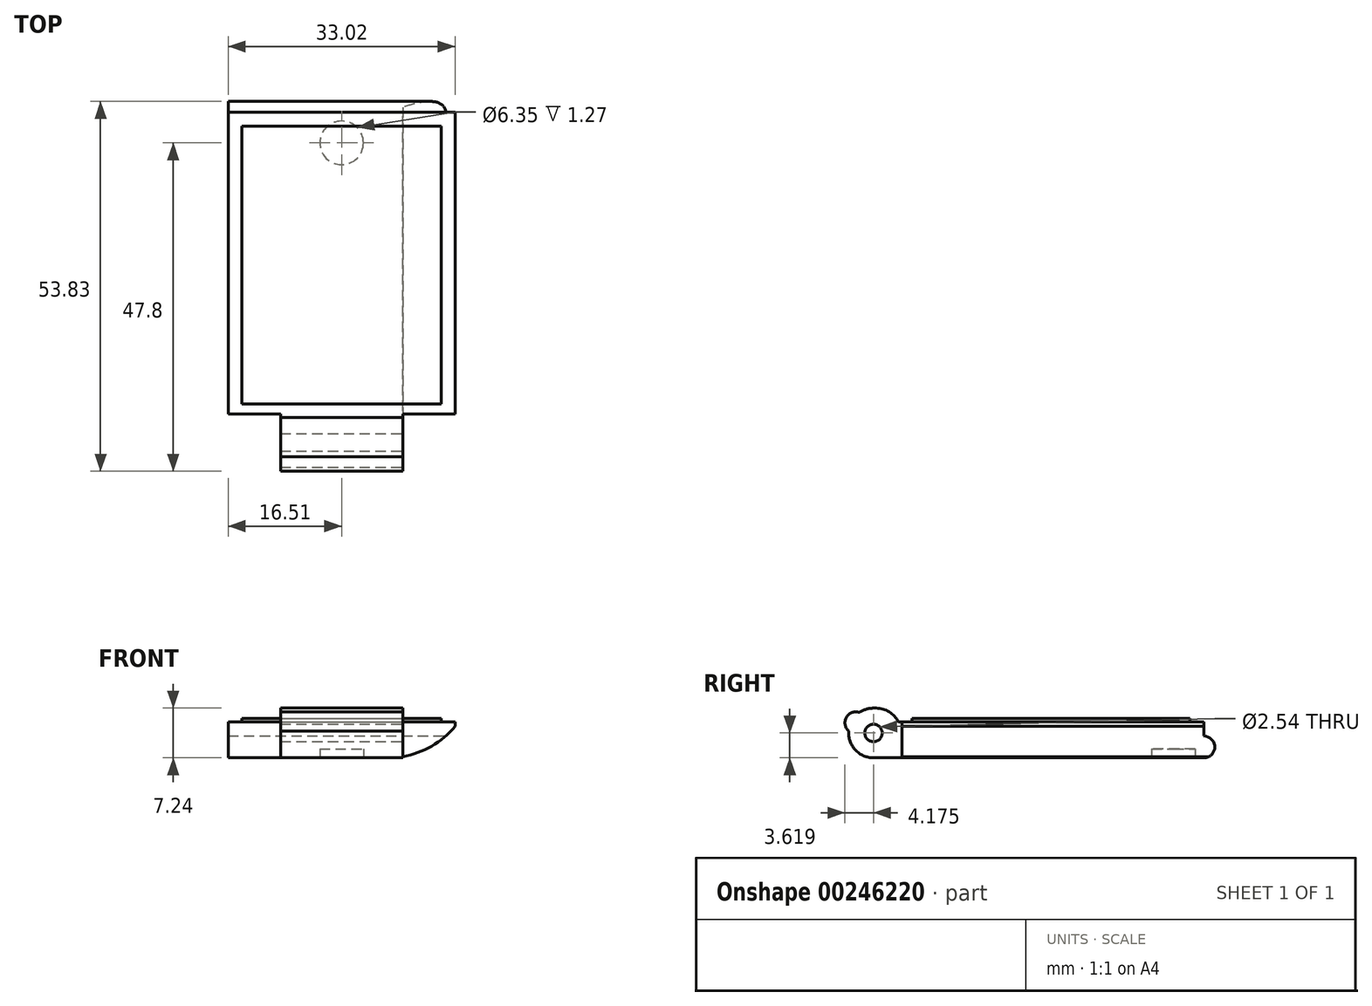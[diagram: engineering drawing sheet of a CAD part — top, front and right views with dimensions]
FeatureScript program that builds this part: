
annotation { "Feature Type Name" : "Feature", "Feature Type Description" : "" }
export const myFeature = defineFeature(function(context is Context, id is Id, definition is map)
    precondition{}
    {
        {
            var Q0;
            Q0=qCreatedBy(makeId("Top.planeOp"),FACE);
            var sketch = newSketch(context, id + "F0", { "sketchPlane" : qUnion([Q0])});
            skLineSegment(sketch, "E0.bottom", {"start": v(-16.51, 22.23) * mm, "end": v(16.51, 22.23) * mm});
            skLineSegment(sketch, "E0.top", {"start": v(-16.51, -22.23) * mm, "end": v(16.51, -22.23) * mm});
            skLineSegment(sketch, "E0.left", {"start": v(-16.51, 22.23) * mm, "end": v(-16.51, -22.23) * mm});
            skLineSegment(sketch, "E0.right", {"start": v(16.51, 22.23) * mm, "end": v(16.51, -22.23) * mm});
            skPoint(sketch, "E0.middle", {"position": v(0, 0) * mm});
            skSolve(sketch);
        }
        {
            var Q0;
            Q0 = qSketchRegion(id + "F0", true);
            extrude(context, id + "F1", {"entities" : qUnion([Q0]), "depth" : 5.7 * mm});
        }
        {
            var Q0;
            Q0=makeQuery(id+"F1.opExtrude","SWEPT_FACE",FACE,{"disambiguationData":[OSD([sQuery(id+"F0.wireOp",EDGE,"E0.top")])]});
            var sketch = newSketch(context, id + "F2", { "sketchPlane" : qUnion([Q0])});
            skLineSegment(sketch, "E1.bottom", {"start": v(-8.9, 7.24) * mm, "end": v(8.89, 7.24) * mm});
            skLineSegment(sketch, "E1.top", {"start": v(-8.9, 0) * mm, "end": v(8.9, 0) * mm});
            skLineSegment(sketch, "E1.left", {"start": v(-8.9, 7.24) * mm, "end": v(-8.9, 0) * mm});
            skLineSegment(sketch, "E1.right", {"start": v(8.9, 7.24) * mm, "end": v(8.9, 0) * mm});
            skSolve(sketch);
        }
        {
            var Q0;
            Q0 = qSketchRegion(id + "F2", true);
            extrude(context, id + "F3", {"entities" : qUnion([Q0]), "operationType" : NewBodyOperationType.ADD, "depth" : 7.24 * mm});
        }
        {
            var Q0;
            Q0=makeQuery(id+"F3.opExtrude","SWEPT_FACE",FACE,{"disambiguationData":[OSD([sQuery(id+"F2.wireOp",EDGE,"E1.right")])]});
            var sketch = newSketch(context, id + "F4", { "sketchPlane" : qUnion([Q0])});
            skCircle(sketch, "E2", {"center": v(-25.84, 3.62) * mm, "radius": 1.27 * mm});
            skPoint(sketch, "E2.centerSnap0", {"position": v(-29.46, 3.62) * mm});
            skPoint(sketch, "E2.centerSnap1", {"position": v(-25.84, 7.24) * mm});
            skSolve(sketch);
        }
        {
            var Q0;
            Q0 = qSketchRegion(id + "F4", true);
            extrude(context, id + "F5", {"entities" : qUnion([Q0]), "operationType" : NewBodyOperationType.REMOVE, "oppositeDirection" : true, "depth" : 19.05 * mm});
        }
        {
            var Q0;
            Q0=makeQuery(id+"F1.opExtrude","CAP_FACE",FACE,{"disambiguationData":[OSD([sQuery(id+"F0.wireOp",EDGE,"E0.bottom"),sQuery(id+"F0.wireOp",EDGE,"E0.top"),sQuery(id+"F0.wireOp",EDGE,"E0.left"),sQuery(id+"F0.wireOp",EDGE,"E0.right")])],"isStart":false});
            var sketch = newSketch(context, id + "F6", { "sketchPlane" : qUnion([Q0])});
            skLineSegment(sketch, "E3.bottom", {"start": v(-16.51, 22.23) * mm, "end": v(16.51, 22.23) * mm});
            skLineSegment(sketch, "E3.top", {"start": v(-16.51, -22.23) * mm, "end": v(16.51, -22.23) * mm});
            skLineSegment(sketch, "E3.left", {"start": v(-16.51, 22.23) * mm, "end": v(-16.51, -22.23) * mm});
            skLineSegment(sketch, "E3.right", {"start": v(16.51, 22.23) * mm, "end": v(16.51, -22.23) * mm});
            skLineSegment(sketch, "E4.0", {"start": v(-14.51, 20.23) * mm, "end": v(14.5, 20.23) * mm});
            skLineSegment(sketch, "E4.1", {"start": v(-14.51, 20.23) * mm, "end": v(-14.5, -20.23) * mm});
            skLineSegment(sketch, "E4.2", {"start": v(-14.5, -20.23) * mm, "end": v(14.51, -20.23) * mm});
            skLineSegment(sketch, "E4.3", {"start": v(14.5, 20.23) * mm, "end": v(14.51, -20.23) * mm});
            skSolve(sketch);
        }
        {
            var Q0;
            Q0 = qSketchRegion(id + "F6", true);
            extrude(context, id + "F7", {"entities" : qUnion([Q0]), "operationType" : NewBodyOperationType.REMOVE, "oppositeDirection" : true, "depth" : 0.5 * mm});
        }
        {
            var Q0;
            Q0=makeQuery(id+"F1.opExtrude","SWEPT_FACE",FACE,{"disambiguationData":[OSD([sQuery(id+"F0.wireOp",EDGE,"E0.right")])]});
            var sketch = newSketch(context, id + "F8", { "sketchPlane" : qUnion([Q0])});
            skArc(sketch, "E5", {"start": v(22.23, 0) * mm, "mid": v(23.81, 1.59) * mm, "end": v(22.23, 3.18) * mm});
            skLineSegment(sketch, "E6", {"start": v(22.23, 3.18) * mm, "end": v(22.23, 0) * mm});
            skSolve(sketch);
        }
        {
            var Q0;
            Q0 = qSketchRegion(id + "F8", true);
            var Q1;
            Q1=makeQuery(id+"F1.opExtrude","SWEPT_FACE",FACE,{"disambiguationData":[OSD([sQuery(id+"F0.wireOp",EDGE,"E0.left")])]});
            extrude(context, id + "F9", {"entities" : qUnion([Q0]), "operationType" : NewBodyOperationType.ADD, "endBound" : BoundingType.UP_TO_SURFACE, "oppositeDirection" : true, "endBoundEntityFace" : qUnion([Q1]), "depth" : 31.75 * mm});
        }
        {
            var Q0;
            Q0=makeQuery(id+"F3.opExtrude","CAP_EDGE",EDGE,{"disambiguationData":[OSD([sQuery(id+"F2.wireOp",EDGE,"E1.bottom")])],"isStart":false});
            var Q1;
            Q1=makeQuery(id+"F3.opExtrude","CAP_EDGE",EDGE,{"disambiguationData":[OSD([sQuery(id+"F2.wireOp",EDGE,"E1.top")])],"isStart":false});
            var Q2;
            Q2=makeQuery(id+"F3.opExtrude","CAP_EDGE",EDGE,{"disambiguationData":[OSD([sQuery(id+"F2.wireOp",EDGE,"E1.bottom")])],"isStart":true});
            fillet(context, id + "F10", {"entities" : qUnion([Q0, Q1, Q2]), "radius" : 3.62 * mm, "tangentPropagation" : true, "allowEdgeOverflow" : false});
        }
        {
            var Q0;
            Q0=makeQuery(id+"F3.boolean.opBoolean","MERGE",FACE,{"derivedFrom":[makeQuery(id+"F1.opExtrude","CAP_FACE",FACE,{"disambiguationData":[OSD([sQuery(id+"F0.wireOp",EDGE,"E0.bottom"),sQuery(id+"F0.wireOp",EDGE,"E0.top"),sQuery(id+"F0.wireOp",EDGE,"E0.left"),sQuery(id+"F0.wireOp",EDGE,"E0.right")])],"isStart":true}),makeQuery(id+"F3.opExtrude","SWEPT_FACE",FACE,{"disambiguationData":[OSD([sQuery(id+"F2.wireOp",EDGE,"E1.top")])]})]});
            var sketch = newSketch(context, id + "F11", { "sketchPlane" : qUnion([Q0])});
            skCircle(sketch, "E7", {"center": v(0, -17.78) * mm, "radius": 3.18 * mm});
            skSolve(sketch);
        }
        {
            var Q0;
            Q0 = qSketchRegion(id + "F11", true);
            extrude(context, id + "F12", {"entities" : qUnion([Q0]), "operationType" : NewBodyOperationType.REMOVE, "oppositeDirection" : true, "depth" : 1.27 * mm});
        }
        {
            var Q0;
            Q0=makeQuery(id+"F3.opExtrude","SWEPT_FACE",FACE,{"disambiguationData":[OSD([sQuery(id+"F2.wireOp",EDGE,"E1.right")])]});
            var sketch = newSketch(context, id + "F13", { "sketchPlane" : qUnion([Q0])});
            skLineSegment(sketch, "E8", {"start": v(-25.84, 3.62) * mm, "end": v(-25.84, 13.68) * mm, "construction": true});
            skLineSegment(sketch, "E9", {"start": v(-25.84, 3.62) * mm, "end": v(-33.62, 8.1) * mm, "construction": true});
            skLineSegment(sketch, "E10", {"start": v(-28.98, 5.43) * mm, "end": v(-31.04, 1.86) * mm, "construction": true});
            skLineSegment(sketch, "E11", {"start": v(-28.98, 5.43) * mm, "end": v(-26.93, 8.98) * mm, "construction": true});
            skArc(sketch, "E12", {"start": v(-27.9, 6.6) * mm, "mid": v(-29.8, 5.9) * mm, "end": v(-29.45, 3.9) * mm});
            skLineSegment(sketch, "E13", {"start": v(-28.98, 5.43) * mm, "end": v(-28.43, 5.11) * mm, "construction": true});
            skArc(sketch, "E14", {"start": v(-27.9, 6.6) * mm, "mid": v(-28.98, 5.43) * mm, "end": v(-29.45, 3.9) * mm});
            skSolve(sketch);
        }
        {
            var Q0;
            Q0 = qSketchRegion(id + "F13", true);
            extrude(context, id + "F14", {"entities" : qUnion([Q0]), "operationType" : NewBodyOperationType.ADD, "oppositeDirection" : true, "depth" : 17.78 * mm});
        }
        {
            var Q0;
            {var subQ0=sQuery(id+"F0.wireOp",EDGE,"E0.left");var subQ4=sQuery(id+"F0.wireOp",EDGE,"E0.top");Q0=makeQuery(id+"F3.boolean.opBoolean","SPLIT",FACE,{"disambiguationData":[TD([makeQuery(id+"F1.opExtrude","SWEPT_FACE",FACE,{"disambiguationData":[OSD([subQ0])]})])],"derivedFrom":makeQuery(id+"F1.opExtrude","SWEPT_FACE",FACE,{"disambiguationData":[OSD([subQ4])]})});}
            var sketch = newSketch(context, id + "F15", { "sketchPlane" : qUnion([Q0])});
            skLineSegment(sketch, "E15.bottom", {"start": v(-16.51, 5.22) * mm, "end": v(-8.9, 5.22) * mm});
            skLineSegment(sketch, "E15.top", {"start": v(-16.51, 0) * mm, "end": v(-8.9, 0) * mm});
            skLineSegment(sketch, "E15.left", {"start": v(-16.51, 5.22) * mm, "end": v(-16.51, 0) * mm});
            skLineSegment(sketch, "E15.right", {"start": v(-8.9, 5.22) * mm, "end": v(-8.9, 0) * mm});
            skLineSegment(sketch, "E16.bottom", {"start": v(16.51, 5.22) * mm, "end": v(8.89, 5.21) * mm});
            skLineSegment(sketch, "E16.top", {"start": v(16.51, 0) * mm, "end": v(8.9, 0) * mm});
            skLineSegment(sketch, "E16.left", {"start": v(16.51, 5.22) * mm, "end": v(16.51, 0) * mm});
            skLineSegment(sketch, "E16.right", {"start": v(8.9, 5.21) * mm, "end": v(8.9, 0) * mm});
            skSolve(sketch);
        }
        {
            var Q0;
            Q0 = qSketchRegion(id + "F15", true);
            extrude(context, id + "F16", {"entities" : qUnion([Q0]), "operationType" : NewBodyOperationType.REMOVE, "oppositeDirection" : true, "depth" : 0.5 * mm});
        }
        {
            var Q0;
            Q0=makeQuery(id+"F16.boolean.opBoolean","COPY",FACE,{"derivedFrom":makeQuery(id+"F16.opExtrude","CAP_FACE",FACE,{"disambiguationData":[OSD([sQuery(id+"F15.wireOp",EDGE,"E15.bottom"),sQuery(id+"F15.wireOp",EDGE,"E15.top"),sQuery(id+"F15.wireOp",EDGE,"E15.left"),sQuery(id+"F15.wireOp",EDGE,"E15.right")])],"isStart":false})});
            var sketch = newSketch(context, id + "F17", { "sketchPlane" : qUnion([Q0])});
            skLineSegment(sketch, "E17.bottom", {"start": v(-16.51, 0) * mm, "end": v(-18.44, 0) * mm, "construction": true});
            skLineSegment(sketch, "E17.top", {"start": v(-16.54, 1.31) * mm, "end": v(-18.47, 1.31) * mm, "construction": true});
            skLineSegment(sketch, "E17.right", {"start": v(-18.44, 0) * mm, "end": v(-18.47, 1.31) * mm, "construction": true});
            skArc(sketch, "E18", {"start": v(-16.05, 5.21) * mm, "mid": v(-12.9, 2.17) * mm, "end": v(-8.9, 0.38) * mm, "construction": true});
            skLineSegment(sketch, "E19", {"start": v(-8.9, 0) * mm, "end": v(-16.51, 0) * mm, "construction": true});
            skLineSegment(sketch, "E20", {"start": v(-16.51, 5.22) * mm, "end": v(-16.05, 5.22) * mm, "construction": true});
            skLineSegment(sketch, "E21", {"start": v(-8.9, 0.38) * mm, "end": v(-8.9, 0) * mm, "construction": true});
            skPoint(sketch, "E22.orphan", {"position": v(-5.8, 0) * mm});
            skLineSegment(sketch, "E23", {"start": v(-16.51, 5.22) * mm, "end": v(-16.51, 0) * mm, "construction": true});
            skLineSegment(sketch, "E24", {"start": v(0, 0) * mm, "end": v(0, 15.07) * mm, "construction": true});
            skLineSegment(sketch, "E25.MirrorCS", {"start": v(18.44, 0) * mm, "end": v(18.47, 1.31) * mm, "construction": true});
            skLineSegment(sketch, "E26.MirrorCS", {"start": v(16.51, 5.22) * mm, "end": v(16.05, 5.22) * mm, "construction": true});
            skLineSegment(sketch, "E27.MirrorCS", {"start": v(8.9, 0.38) * mm, "end": v(8.9, 0) * mm, "construction": true});
            skLineSegment(sketch, "E28.MirrorCS", {"start": v(16.54, 1.31) * mm, "end": v(18.47, 1.31) * mm, "construction": true});
            skLineSegment(sketch, "E29.MirrorCS", {"start": v(16.51, 0) * mm, "end": v(18.44, 0) * mm, "construction": true});
            skArc(sketch, "E30.MirrorCS", {"start": v(16.05, 5.21) * mm, "mid": v(12.9, 2.17) * mm, "end": v(8.9, 0.38) * mm, "construction": true});
            skLineSegment(sketch, "E31.MirrorCS", {"start": v(8.9, 0) * mm, "end": v(16.51, 0) * mm});
            skLineSegment(sketch, "E32.MirrorCS", {"start": v(16.51, 5.22) * mm, "end": v(16.51, 0) * mm});
            skArc(sketch, "E33", {"start": v(8.9, 0) * mm, "mid": v(13.18, 1.91) * mm, "end": v(16.51, 5.22) * mm});
            skSolve(sketch);
        }
        {
            var Q0;
            Q0=makeQuery(id+"F16.boolean.opBoolean","COPY",FACE,{"derivedFrom":makeQuery(id+"F16.opExtrude","CAP_FACE",FACE,{"disambiguationData":[OSD([sQuery(id+"F15.wireOp",EDGE,"E16.bottom"),sQuery(id+"F15.wireOp",EDGE,"E16.top"),sQuery(id+"F15.wireOp",EDGE,"E16.left"),sQuery(id+"F15.wireOp",EDGE,"E16.right")])],"isStart":false})});
            var sketch = newSketch(context, id + "F18", { "sketchPlane" : qUnion([Q0])});
            skArc(sketch, "E34", {"start": v(8.89, 0.18) * mm, "mid": v(13.1, 1.7) * mm, "end": v(16.51, 4.58) * mm});
            skLineSegment(sketch, "E35", {"start": v(16.51, 0) * mm, "end": v(16.51, 4.58) * mm});
            skLineSegment(sketch, "E36", {"start": v(16.51, 0) * mm, "end": v(8.9, 0) * mm});
            skLineSegment(sketch, "E37", {"start": v(8.9, 0) * mm, "end": v(8.9, 0.18) * mm});
            skSolve(sketch);
        }
        {
            var Q0;
            Q0 = qSketchRegion(id + "F18", true);
            extrude(context, id + "F19", {"entities" : qUnion([Q0]), "operationType" : NewBodyOperationType.REMOVE, "oppositeDirection" : true, "depth" : 76.2 * mm});
        }
    });
